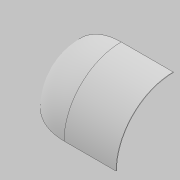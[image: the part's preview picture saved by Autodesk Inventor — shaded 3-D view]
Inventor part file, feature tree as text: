
AUTODESK INVENTOR PART (.ipt)
format: ipt  version: 2021 (Build 250183000, 183)  size: 125,952 bytes
history: native  units: mm
features: sketch x2, revolve x1, extrude x1
ambient origin geometry x8: Origin, YZ Plane, XZ Plane, XY Plane, X Axis, Y Axis, Z Axis, Center Point
bodies: Body1 (feature_tree)
feature tree (4):
  revolve  "Revolution1"  [1 undecoded]
  extrude  "Extrusion2"  TaperAngle=0.0deg  [1 undecoded]
  sketch  "Sketch1"  dims[d0=10.0mm d1=990.0mm]
  sketch  "Sketch2"  dims[d2=0.0mm d3=0.0mm d6=90.0deg d9=900.0mm d10=0.0mm]
note: 2 required parameter values undecoded (feature->parameter linkage not recoverable at this tier; creation-order binding heuristic only, values carry confidence <= 0.55)